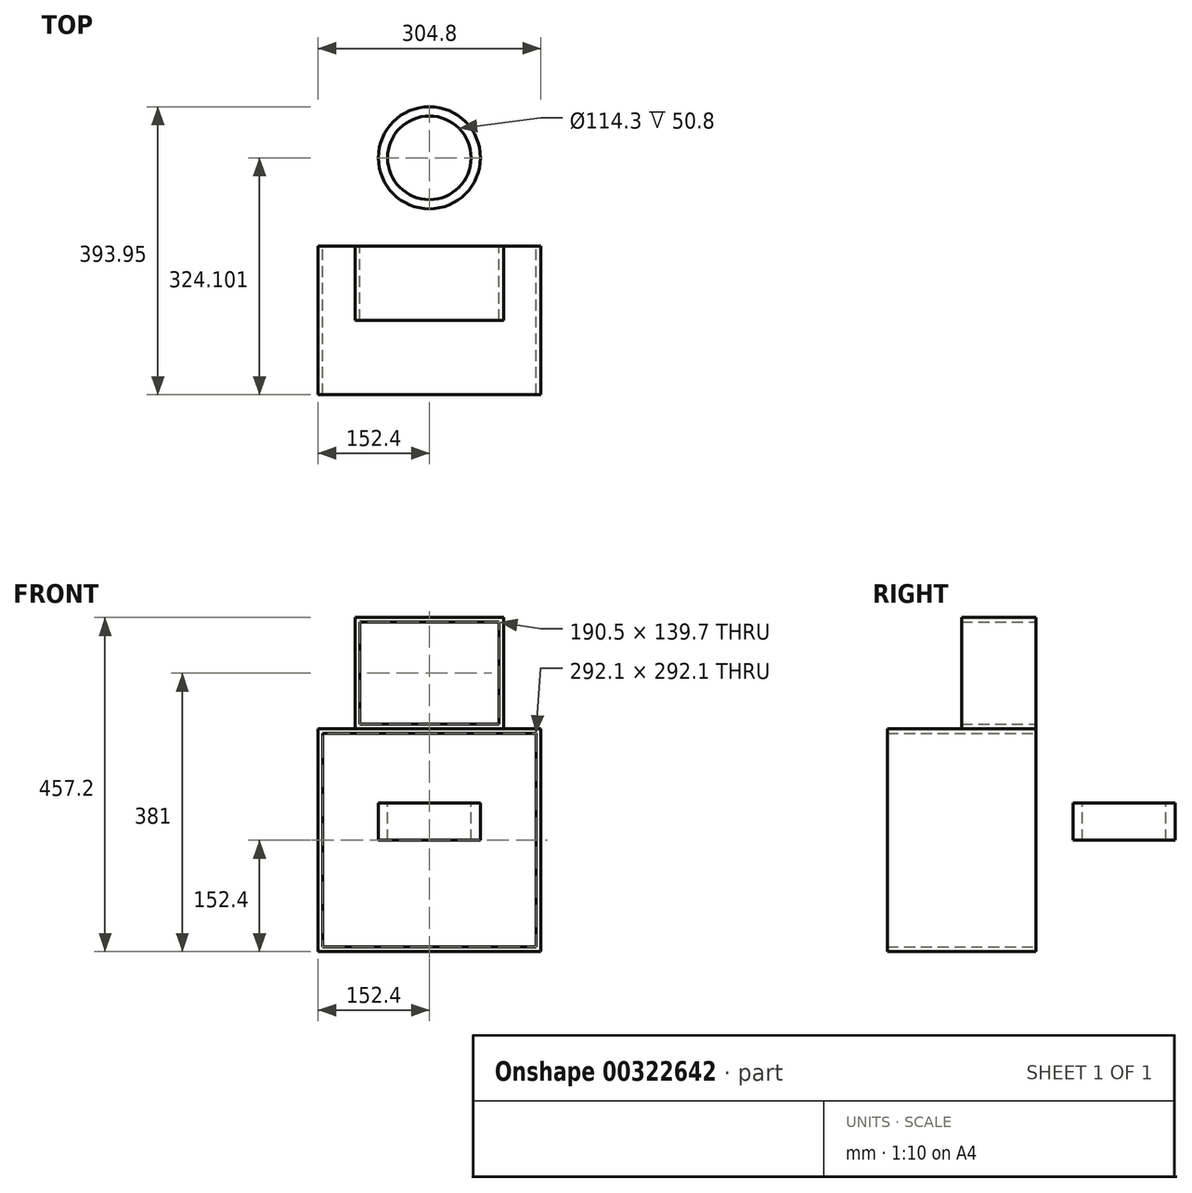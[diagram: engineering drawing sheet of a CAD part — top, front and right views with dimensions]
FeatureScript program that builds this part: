
annotation { "Feature Type Name" : "Feature", "Feature Type Description" : "" }
export const myFeature = defineFeature(function(context is Context, id is Id, definition is map)
    precondition{}
    {
        {
            var Q0;
            Q0=qCreatedBy(makeId("Front.planeOp"),FACE);
            var sketch = newSketch(context, id + "F0", { "sketchPlane" : qUnion([Q0])});
            skLineSegment(sketch, "E0.bottom", {"start": v(-101.6, 0) * mm, "end": v(101.6, 0) * mm});
            skLineSegment(sketch, "E0.top", {"start": v(-101.6, 152.4) * mm, "end": v(101.6, 152.4) * mm});
            skLineSegment(sketch, "E0.left", {"start": v(-101.6, 0) * mm, "end": v(-101.6, 152.4) * mm});
            skLineSegment(sketch, "E0.right", {"start": v(101.6, 0) * mm, "end": v(101.6, 152.4) * mm});
            skLineSegment(sketch, "E1.bottom", {"start": v(-95.25, 6.35) * mm, "end": v(95.25, 6.35) * mm});
            skLineSegment(sketch, "E1.top", {"start": v(-95.25, 146.05) * mm, "end": v(95.25, 146.05) * mm});
            skLineSegment(sketch, "E1.left", {"start": v(-95.25, 6.35) * mm, "end": v(-95.25, 146.05) * mm});
            skLineSegment(sketch, "E1.right", {"start": v(95.25, 6.35) * mm, "end": v(95.25, 146.05) * mm});
            skLineSegment(sketch, "E2.bottom", {"start": v(-152.4, 0) * mm, "end": v(152.4, 0) * mm});
            skLineSegment(sketch, "E2.top", {"start": v(-152.4, -304.8) * mm, "end": v(152.4, -304.8) * mm});
            skLineSegment(sketch, "E2.left", {"start": v(-152.4, 0) * mm, "end": v(-152.4, -304.8) * mm});
            skLineSegment(sketch, "E2.right", {"start": v(152.4, 0) * mm, "end": v(152.4, -304.8) * mm});
            skLineSegment(sketch, "E3.bottom", {"start": v(-146.05, -6.35) * mm, "end": v(146.05, -6.35) * mm});
            skLineSegment(sketch, "E3.top", {"start": v(-146.05, -298.45) * mm, "end": v(146.05, -298.45) * mm});
            skLineSegment(sketch, "E3.left", {"start": v(-146.05, -6.35) * mm, "end": v(-146.05, -298.45) * mm});
            skLineSegment(sketch, "E3.right", {"start": v(146.05, -6.35) * mm, "end": v(146.05, -298.45) * mm});
            skLineSegment(sketch, "E4", {"start": v(0, 152.4) * mm, "end": v(0, 146.05) * mm, "construction": true});
            skLineSegment(sketch, "E5", {"start": v(-101.6, 76.2) * mm, "end": v(-95.25, 76.2) * mm, "construction": true});
            skLineSegment(sketch, "E6", {"start": v(0, 0) * mm, "end": v(0, -6.35) * mm, "construction": true});
            skLineSegment(sketch, "E7", {"start": v(-152.4, -152.4) * mm, "end": v(-146.05, -152.4) * mm, "construction": true});
            skLineSegment(sketch, "E8", {"start": v(95.25, 76.2) * mm, "end": v(101.6, 76.2) * mm, "construction": true});
            skLineSegment(sketch, "E9", {"start": v(0, 0) * mm, "end": v(0, 6.35) * mm, "construction": true});
            skLineSegment(sketch, "E10", {"start": v(146.05, -152.4) * mm, "end": v(152.4, -152.4) * mm, "construction": true});
            skLineSegment(sketch, "E11", {"start": v(0, -298.45) * mm, "end": v(0, -304.8) * mm, "construction": true});
            skSolve(sketch);
        }
        {
            var Q0;
            Q0=makeQuery(id+"F0.imprint","IMPRINT",FACE,{"disambiguationData":[TD([[makeQuery(id+"F0.imprint","IMPRINT",EDGE,{"derivedFrom":sQuery(id+"F0.wireOp",EDGE,"E0.top")}),-1.0]])]});
            extrude(context, id + "F1", {"entities" : qUnion([Q0]), "depth" : 101.6 * mm});
        }
        {
            var Q0;
            Q0=makeQuery(id+"F0.imprint","IMPRINT",FACE,{"disambiguationData":[TD([[makeQuery(id+"F0.imprint","IMPRINT",EDGE,{"derivedFrom":sQuery(id+"F0.wireOp",EDGE,"E2.top")}),1.0]])]});
            extrude(context, id + "F2", {"entities" : qUnion([Q0]), "operationType" : NewBodyOperationType.ADD, "depth" : 203.2 * mm});
        }
        {
            var Q0;
            Q0=qCreatedBy(makeId("Top.planeOp"),FACE);
            cPlane(context, id + "F3", {"entities" : qUnion([Q0]), "cplaneType" : CPlaneType.OFFSET, "offset" : 101.6 * mm, "oppositeDirection" : true, "width" : 152.4 * mm, "height" : 152.4 * mm});
        }
        {
            var Q0;
            Q0=qCreatedBy(id+"F3.planeOp",FACE);
            var sketch = newSketch(context, id + "F4", { "sketchPlane" : qUnion([Q0])});
            skCircle(sketch, "E12", {"center": v(0, 120.9) * mm, "radius": 57.15 * mm});
            skCircle(sketch, "E13", {"center": v(0, 120.9) * mm, "radius": 69.85 * mm});
            skSolve(sketch);
        }
        {
            var Q0;
            Q0=makeQuery(id+"F4.imprint","IMPRINT",FACE,{"disambiguationData":[TD([[makeQuery(id+"F4.imprint","IMPRINT",EDGE,{"derivedFrom":sQuery(id+"F4.wireOp",EDGE,"E12")}),-1.0]])]});
            var Q1;
            Q1 = qConstructionFilter(qBodyType(qCreatedBy(id + "F4" ,EDGE), BodyType.WIRE), ConstructionObject.NO);
            extrude(context, id + "F5", {"entities" : qUnion([Q0]), "surfaceEntities" : qUnion([Q1]), "oppositeDirection" : true, "depth" : 50.8 * mm});
        }
    });
